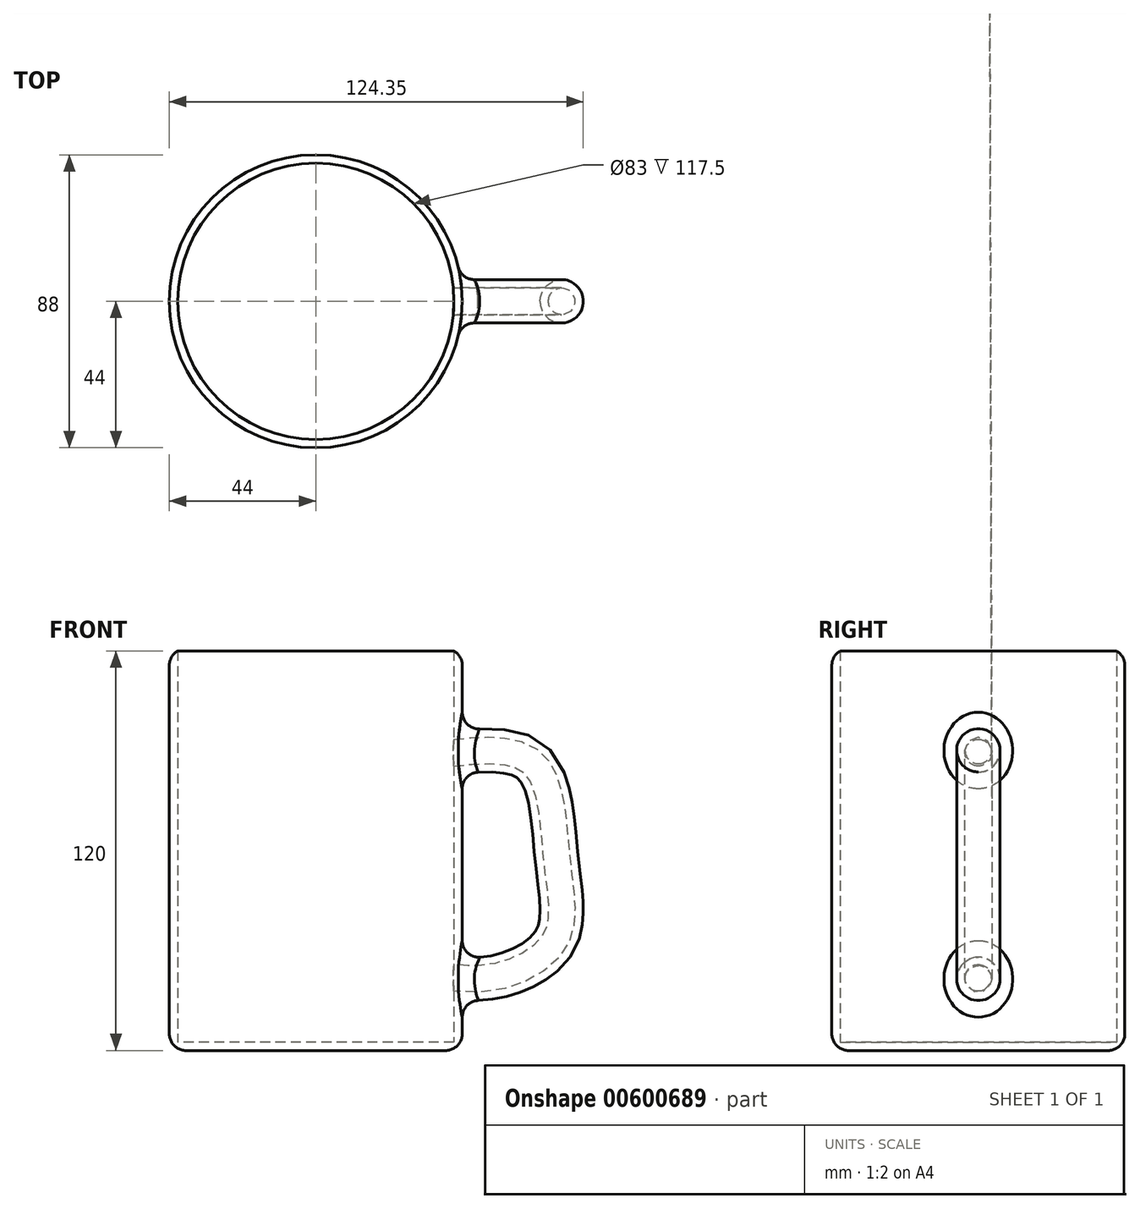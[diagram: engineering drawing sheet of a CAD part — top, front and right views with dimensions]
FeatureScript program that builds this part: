
annotation { "Feature Type Name" : "Feature", "Feature Type Description" : "" }
export const myFeature = defineFeature(function(context is Context, id is Id, definition is map)
    precondition{}
    {
        {
            var Q0;
            Q0=qCreatedBy(makeId("Top.planeOp"),FACE);
            var sketch = newSketch(context, id + "F0", { "sketchPlane" : qUnion([Q0])});
            skCircle(sketch, "E0", {"center": v(0, 0) * mm, "radius": 44 * mm});
            skSolve(sketch);
        }
        {
            var Q0;
            Q0 = qSketchRegion(id + "F0", true);
            extrude(context, id + "F1", {"entities" : qUnion([Q0]), "depth" : 120 * mm, "offsetDistance" : 25 * mm});
        }
        {
            var Q0;
            Q0=qCreatedBy(makeId("Front.planeOp"),FACE);
            var sketch = newSketch(context, id + "F2", { "sketchPlane" : qUnion([Q0])});
            skFitSpline(sketch, "E1", {"points": [v(35.5, 89.18) * mm, v(65.53, 86.65) * mm, v(72.83, 57.35) * mm, v(72.41, 33.07) * mm, v(53.58, 21.57) * mm, v(32.12, 22.89) * mm], "startDerivative": vector(165.47, 21.26) * mm, "endDerivative": vector(-114.3, 21.87) * mm});
            skSolve(sketch);
        }
        {
            var Q0;
            Q0=qCreatedBy(makeId("Right.planeOp"),FACE);
            cPlane(context, id + "F3", {"entities" : qUnion([Q0]), "cplaneType" : CPlaneType.OFFSET, "offset" : 44 * mm, "width" : 150 * mm, "height" : 150 * mm});
        }
        {
            var Q0;
            Q0=qCreatedBy(id+"F3.planeOp",FACE);
            var sketch = newSketch(context, id + "F4", { "sketchPlane" : qUnion([Q0])});
            skCircle(sketch, "E2", {"center": v(0, 89.71) * mm, "radius": 6.51 * mm});
            skSolve(sketch);
        }
        {
            var Q0;
            Q0=makeQuery(id+"F4.imprint","IMPRINT",FACE,{"disambiguationData":[TD([[makeQuery(id+"F4.imprint","IMPRINT",EDGE,{"derivedFrom":sQuery(id+"F4.wireOp",EDGE,"E2")}),1.0]])]});
            var Q1;
            Q1=sQuery(id+"F2.wireOp",EDGE,"E1");
            sweep(context, id + "F5", {"operationType" : NewBodyOperationType.ADD, "profiles" : qUnion([Q0]), "path" : qUnion([Q1])});
        }
        {
            var Q0;
            Q0=makeQuery(id+"F1.opExtrude","CAP_FACE",FACE,{"disambiguationData":[OSD([sQuery(id+"F0.wireOp",EDGE,"E0")])],"isStart":false});
            shell(context, id + "F6", {"entities" : qUnion([Q0]), "thickness" : 2.5 * mm});
        }
        {
            var Q0;
            Q0=makeQuery(id+"F1.opExtrude","CAP_EDGE",EDGE,{"disambiguationData":[OSD([sQuery(id+"F0.wireOp",EDGE,"E0")])],"isStart":false});
            var Q1;
            Q1=makeQuery(id+"F1.opExtrude","CAP_EDGE",EDGE,{"disambiguationData":[OSD([sQuery(id+"F0.wireOp",EDGE,"E0")])],"isStart":true});
            var Q2;
            Q2=makeQuery(id+"F1.opExtrude","SWEPT_FACE",FACE,{"disambiguationData":[OSD([sQuery(id+"F0.wireOp",EDGE,"E0")])]});
            fillet(context, id + "F7", {"entities" : qUnion([Q0, Q1, Q2]), "radius" : 5 * mm, "tangentPropagation" : true, "allowEdgeOverflow" : false});
        }
    });
